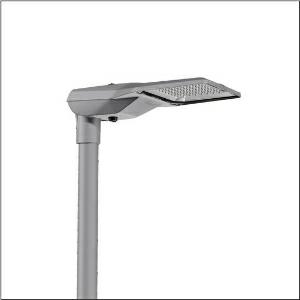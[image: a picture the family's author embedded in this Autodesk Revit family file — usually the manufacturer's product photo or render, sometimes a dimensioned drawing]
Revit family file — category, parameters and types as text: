
# Revit family: streetlight_sl_21_midi___st0_8a_5xe3c43t08mb_e12c
name_source: partatom
category: Lighting Fixtures
units: mm (PartAtom-declared; Revit-internal decimal feet)

## family parameters
Cut with Voids When Loaded = No
Host = Face
Light Source = No
Part Type = Normal
Room Calculation Point = No
Round Connector Dimension = Use Diameter
Shared = No

## types (1)
- --- (1 x LED, 20180 lm, 147 W, 4000K)
    Apparent Load = 147 VA
    CIE Flux Codes = 38 75 97 100 100
    Color Rendering = 70
    Color Temperature = 4000K
    Default Elevation = 1800 mm
    Description = Streetlight SL 21 midi, mast luminaire, primary light control with lens, of PMMA, primary optical cover: cover, of toughened safety glass, transparent, light distribution: ST0.8a, light emission: direct distribution, primary light characteristic: asymmetric, installation type: side-entry, post-top, LED, High Power LED, rated luminous flux: 20.180lm, luminous efficacy: 137lm/W, light colour: 740, colour temperature: 4000K, control gear: D4i, control: overheat protection, constant luminous flux control, time-dependent luminous flux control, flexible luminous flux parameterisation, pre-setting: logarithmic dimming characteristic, mains connection: 230..240V, AC, 50/60Hz, start of lifetime: 147W, end of service life: 155W, reduction: 65W, luminaire housing, of diecast aluminium, powder-coated, Siteco® metallic grey (DB 702S), corrosivity category C5 mid according to DIN EN ISO 12944, please order mast flange separately, inclination adjustable: 0°, 5°, 10°, 15°, sealing non-destructively replaceable, multi-level sealing system, length: 644mm, width: 335mm, height: 110mm, mast flange for spigot size: 42mm (side-entry): 5XC10008XM4, 60/48mm (side-entry/post-top): 5XC10108XM2, 76/60mm (side-entry/post-top): 5XC10108XM1, mounting height: 4..8m, Smart Interface below and above, protection rating (complete): IP66, insulation class (complete): insulation class II (safety insulation), certification: CE, ENEC, ENEC+, VDE, impact resistance: IK10, permissible operating ambient temperature for outdoor applications: -40..+50°C, standard-compliant lighting for roads and squares, packaging unit: 1 piece

Light Distribution: ST0.8a
    Height = 111 mm
    Lamp = 1 x LED
    Lamp Light Flux = 20180 lm
    Lamp Power = 147 W
    Lamp count = 1
    Length = 644 mm
    Luminous efficacy = 137 lm/W
    Manufacturer = Siteco
    ModVariant = No
    Model = 5XE3C43T08MB
    Number of Poles = 1
    OnlyDefault = Yes
    Power Factor = 1
    Product Name = Streetlight SL 21 midi | ST0.8a
    Product group = mast luminaire | pylon top
    ProductGroupID = 6100
    Protection Class = Protection class II
    Protection Degree = IP 66
    RLX_Detail_Level = 1
    RLX_Emergency_Light_Flux = 0 lm
    RLX_Emergency_Type = 0
    RLX_Emergency_Type_DB = No
    RlxData = <blob elided: 27069 chars, md5=bf7a968b>
    Socket = socket
    Standby Power = 0 W
    System Light Flux = 20180 lm
    System Power = 147 W
    Type Comments = factory setting: luminous flux: 100 % | dim-lin: 254 | 750 mA
    Type Image = l_1004304.jpg
    URL = http://relux.com
    VarID = @adj_185990
    Voltage = 0 V
    Weight = 0.00 kg
    Width = 336 mm

## geometry (parser evidence)
native form markers: Blend x4, Sweep x12
no freeform markers — native parametric forms only
